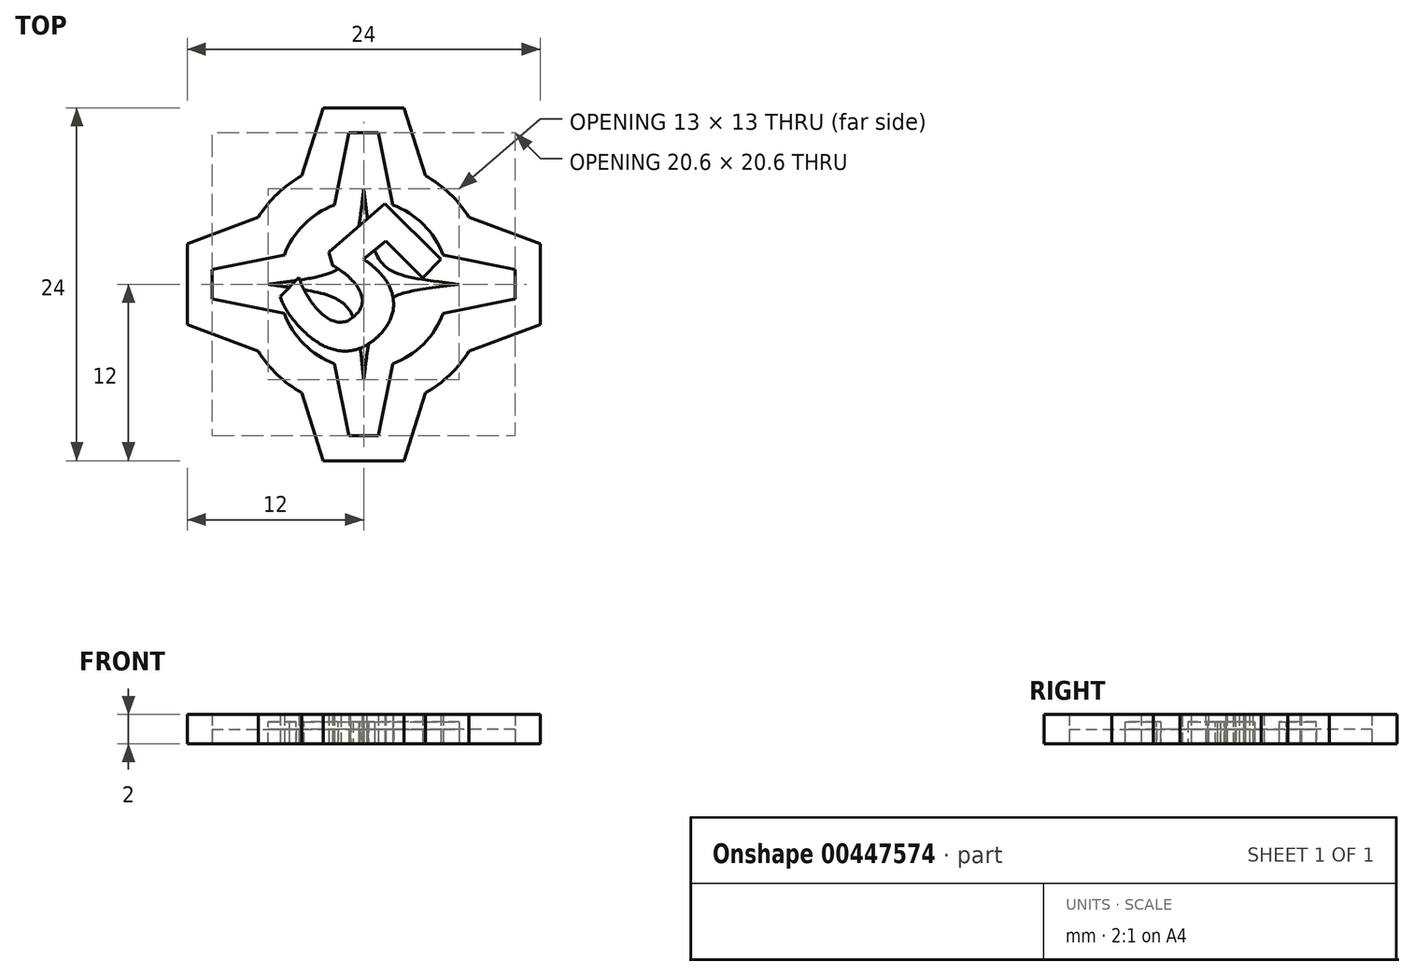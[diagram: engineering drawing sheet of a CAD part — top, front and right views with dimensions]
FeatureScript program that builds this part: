
annotation { "Feature Type Name" : "Feature", "Feature Type Description" : "" }
export const myFeature = defineFeature(function(context is Context, id is Id, definition is map)
    precondition{}
    {
        {
            var Q0;
            Q0=qCreatedBy(makeId("Top.planeOp"),FACE);
            var sketch = newSketch(context, id + "F0", { "sketchPlane" : qUnion([Q0])});
            skArc(sketch, "E0", {"start": v(-4.2, 7.39) * mm, "mid": v(-5.86, 6.16) * mm, "end": v(-7.17, 4.56) * mm});
            skLineSegment(sketch, "E1", {"start": v(-2.75, 12) * mm, "end": v(2.75, 12) * mm});
            skLineSegment(sketch, "E2", {"start": v(2.75, 12) * mm, "end": v(4.2, 7.39) * mm});
            skLineSegment(sketch, "E3", {"start": v(-2.75, 12) * mm, "end": v(-4.2, 7.39) * mm});
            skLineSegment(sketch, "E4", {"start": v(12, 2.75) * mm, "end": v(12, -2.75) * mm});
            skLineSegment(sketch, "E5", {"start": v(12, -2.75) * mm, "end": v(7.17, -4.56) * mm});
            skLineSegment(sketch, "E6", {"start": v(12, 2.75) * mm, "end": v(7.17, 4.56) * mm});
            skLineSegment(sketch, "E7.MirrorCS", {"start": v(-12, 2.75) * mm, "end": v(-7.17, 4.56) * mm});
            skLineSegment(sketch, "E8.MirrorCS", {"start": v(-12, 2.75) * mm, "end": v(-12, -2.75) * mm});
            skLineSegment(sketch, "E9.MirrorCS", {"start": v(-12, -2.75) * mm, "end": v(-7.17, -4.56) * mm});
            skLineSegment(sketch, "E10.MirrorCS", {"start": v(-2.75, -12) * mm, "end": v(-4.2, -7.39) * mm});
            skLineSegment(sketch, "E11.MirrorCS", {"start": v(-2.75, -12) * mm, "end": v(2.75, -12) * mm});
            skLineSegment(sketch, "E12.MirrorCS", {"start": v(2.75, -12) * mm, "end": v(4.2, -7.39) * mm});
            skArc(sketch, "E13", {"start": v(-1.98, 5.4) * mm, "mid": v(-4.07, 4.07) * mm, "end": v(-5.4, 1.98) * mm});
            skArc(sketch, "E14.trimOffspring", {"start": v(-7.17, -4.56) * mm, "mid": v(-5.86, -6.16) * mm, "end": v(-4.2, -7.39) * mm});
            skArc(sketch, "E15.trimOffspring", {"start": v(7.17, 4.56) * mm, "mid": v(5.86, 6.16) * mm, "end": v(4.2, 7.39) * mm});
            skArc(sketch, "E16.trimOffspring", {"start": v(4.2, -7.39) * mm, "mid": v(5.86, -6.16) * mm, "end": v(7.17, -4.56) * mm});
            skLineSegment(sketch, "E17", {"start": v(-1, 10.3) * mm, "end": v(1, 10.3) * mm});
            skLineSegment(sketch, "E18", {"start": v(1, 10.3) * mm, "end": v(1.98, 5.4) * mm});
            skLineSegment(sketch, "E19", {"start": v(-1, 10.3) * mm, "end": v(-1.98, 5.4) * mm});
            skLineSegment(sketch, "E20", {"start": v(10.3, 1) * mm, "end": v(10.3, -1) * mm});
            skLineSegment(sketch, "E21", {"start": v(10.3, -1) * mm, "end": v(5.4, -1.98) * mm});
            skLineSegment(sketch, "E22", {"start": v(10.3, 1) * mm, "end": v(5.4, 1.98) * mm});
            skLineSegment(sketch, "E23.MirrorCS", {"start": v(-1, -10.3) * mm, "end": v(-1.98, -5.4) * mm});
            skLineSegment(sketch, "E24.MirrorCS", {"start": v(-1, -10.3) * mm, "end": v(1, -10.3) * mm});
            skLineSegment(sketch, "E25.MirrorCS", {"start": v(1, -10.3) * mm, "end": v(1.98, -5.4) * mm});
            skLineSegment(sketch, "E26.MirrorCS", {"start": v(-10.3, 1) * mm, "end": v(-5.4, 1.98) * mm});
            skLineSegment(sketch, "E27.MirrorCS", {"start": v(-10.3, 1) * mm, "end": v(-10.3, -1) * mm});
            skLineSegment(sketch, "E28.MirrorCS", {"start": v(-10.3, -1) * mm, "end": v(-5.4, -1.98) * mm});
            skArc(sketch, "E29.trimOffspring", {"start": v(-5.4, -1.98) * mm, "mid": v(-4.07, -4.07) * mm, "end": v(-1.98, -5.4) * mm});
            skArc(sketch, "E30.trimOffspring", {"start": v(1.98, -5.4) * mm, "mid": v(4.07, -4.07) * mm, "end": v(5.4, -1.98) * mm});
            skArc(sketch, "E31.trimOffspring", {"start": v(5.4, 1.98) * mm, "mid": v(4.07, 4.07) * mm, "end": v(1.98, 5.4) * mm});
            skFitSpline(sketch, "E32", {"points": [v(-6.5, 0) * mm, v(0, -6.5) * mm], "startDerivative": vector(17.8, -2.47) * mm, "endDerivative": vector(1.7, -17.03) * mm});
            skFitSpline(sketch, "E33", {"points": [v(0, -6.5) * mm, v(6.5, 0) * mm], "startDerivative": vector(2.16, 17.42) * mm, "endDerivative": vector(17.34, 2.08) * mm});
            skFitSpline(sketch, "E34", {"points": [v(6.5, 0) * mm, v(0, 6.5) * mm], "startDerivative": vector(-17.34, 2.09) * mm, "endDerivative": vector(-2.16, 17.41) * mm});
            skFitSpline(sketch, "E35", {"points": [v(0, 6.5) * mm, v(-6.5, 0) * mm], "startDerivative": vector(-2, -17.27) * mm, "endDerivative": vector(-17.5, -2.23) * mm});
            skText(sketch, "E36", { "text": "5", "fontName": "OpenSans-Bold.ttf"});
            const initialGuessF0  = {"E36": [-0.00644, -0.00063, 0.707, -0.70722, 0.01]};
            skSetInitialGuess(sketch, initialGuessF0);
            skSolve(sketch);
        }
        {
            var Q0;
            Q0=makeQuery(id+"F0.imprint","IMPRINT",FACE,{"disambiguationData":[TD([[makeQuery(id+"F0.imprint","IMPRINT",EDGE,{"derivedFrom":sQuery(id+"F0.wireOp",EDGE,"E0")}),1.0]])]});
            var Q1;
            {var subQ5=sQuery(id+"F0.wireOp",EDGE,"E36.sketch_text.stroke-14");Q1=makeQuery(id+"F0.imprint","IMPRINT",FACE,{"disambiguationData":[TD([[makeQuery(id+"F0.imprint","IMPRINT",EDGE,{"derivedFrom":subQ5}),-1.0]])]});}
            var Q2;
            {var subQ6=sQuery(id+"F0.wireOp",EDGE,"E36.sketch_text.stroke-9");Q2=makeQuery(id+"F0.imprint","IMPRINT",FACE,{"disambiguationData":[TD([[makeQuery(id+"F0.imprint","IMPRINT",EDGE,{"derivedFrom":subQ6}),-1.0]])]});}
            var Q3;
            {var subQ5=sQuery(id+"F0.wireOp",EDGE,"E36.sketch_text.stroke-12");Q3=makeQuery(id+"F0.imprint","IMPRINT",FACE,{"disambiguationData":[TD([[makeQuery(id+"F0.imprint","IMPRINT",EDGE,{"derivedFrom":subQ5}),-1.0]])]});}
            var Q4;
            {var subQ5=sQuery(id+"F0.wireOp",EDGE,"E36.sketch_text.stroke-1");Q4=makeQuery(id+"F0.imprint","IMPRINT",FACE,{"disambiguationData":[TD([[makeQuery(id+"F0.imprint","IMPRINT",EDGE,{"derivedFrom":subQ5}),-1.0]])]});}
            var Q5;
            {var subQ0=sQuery(id+"F0.wireOp",EDGE,"E36.sketch_text.stroke-3");Q5=makeQuery(id+"F0.imprint","IMPRINT",FACE,{"disambiguationData":[TD([[makeQuery(id+"F0.imprint","IMPRINT",EDGE,{"derivedFrom":subQ0}),-1.0]])]});}
            var Q6;
            {var subQ0=sQuery(id+"F0.wireOp",EDGE,"E36.sketch_text.stroke-5");var subQ1=sQuery(id+"F0.wireOp",EDGE,"E32");var subQ2=makeQuery(id+"F0.imprint","INTERSECT",VERTEX,{"derivedFrom":[subQ1,subQ0]});Q6=makeQuery(id+"F0.imprint","IMPRINT",FACE,{"disambiguationData":[TD([[makeQuery(id+"F0.imprint","IMPRINT",EDGE,{"disambiguationData":[TD([[subQ2,-1.0]])],"derivedFrom":subQ1}),1.0]])]});}
            var Q7;
            {var subQ0=sQuery(id+"F0.wireOp",EDGE,"E36.sketch_text.stroke-6");var subQ1=sQuery(id+"F0.wireOp",EDGE,"E35");var subQ2=makeQuery(id+"F0.imprint","INTERSECT",VERTEX,{"derivedFrom":[subQ1,subQ0]});Q7=makeQuery(id+"F0.imprint","IMPRINT",FACE,{"disambiguationData":[TD([[makeQuery(id+"F0.imprint","IMPRINT",EDGE,{"disambiguationData":[TD([[subQ2,-1.0]])],"derivedFrom":subQ1}),-1.0]])]});}
            extrude(context, id + "F1", {"entities" : qUnion([Q0, Q1, Q2, Q3, Q4, Q5, Q6, Q7]), "depth" : 2 * mm});
        }
        {
            var Q0;
            Q0=makeQuery(id+"F0.imprint","IMPRINT",FACE,{"disambiguationData":[TD([[makeQuery(id+"F0.imprint","IMPRINT",EDGE,{"derivedFrom":sQuery(id+"F0.wireOp",EDGE,"E13")}),1.0]])]});
            var Q1;
            {var subQ10=sQuery(id+"F0.wireOp",EDGE,"E20");Q1=makeQuery(id+"F0.imprint","IMPRINT",FACE,{"disambiguationData":[TD([[makeQuery(id+"F0.imprint","IMPRINT",EDGE,{"derivedFrom":subQ10}),-1.0]])]});}
            var Q2;
            {var subQ0=sQuery(id+"F0.wireOp",EDGE,"E36.sketch_text.stroke-14");var subQ1=sQuery(id+"F0.wireOp",EDGE,"E31.trimOffspring");var subQ2=makeQuery(id+"F0.imprint","INTERSECT",VERTEX,{"disambiguationData":[OD(0.0)],"derivedFrom":[subQ1,subQ0]});Q2=makeQuery(id+"F0.imprint","IMPRINT",FACE,{"disambiguationData":[TD([[makeQuery(id+"F0.imprint","IMPRINT",EDGE,{"disambiguationData":[TD([[subQ2,-1.0]])],"derivedFrom":subQ1}),1.0]])]});}
            extrude(context, id + "F2", {"entities" : qUnion([Q0, Q1, Q2]), "depth" : 1 * mm});
        }
        {
            var Q0;
            {var subQ0=sQuery(id+"F0.wireOp",EDGE,"E35");var subQ1=sQuery(id+"F0.wireOp",EDGE,"E34");var subQ2=makeQuery(id+"F0.imprint","INTERSECT",VERTEX,{"derivedFrom":[subQ1,subQ0]});Q0=makeQuery(id+"F0.imprint","IMPRINT",FACE,{"disambiguationData":[TD([[makeQuery(id+"F0.imprint","IMPRINT",EDGE,{"disambiguationData":[TD([[subQ2,1.0]])],"derivedFrom":subQ1}),1.0]])]});}
            var Q1;
            {var subQ0=sQuery(id+"F0.wireOp",EDGE,"E36.sketch_text.stroke-18");Q1=makeQuery(id+"F0.imprint","IMPRINT",FACE,{"disambiguationData":[TD([[makeQuery(id+"F0.imprint","IMPRINT",EDGE,{"derivedFrom":subQ0}),1.0]])]});}
            var Q2;
            {var subQ10=sQuery(id+"F0.wireOp",EDGE,"E36.sketch_text.stroke-9");Q2=makeQuery(id+"F0.imprint","IMPRINT",FACE,{"disambiguationData":[TD([[makeQuery(id+"F0.imprint","IMPRINT",EDGE,{"derivedFrom":subQ10}),1.0]])]});}
            var Q3;
            {var subQ0=sQuery(id+"F0.wireOp",EDGE,"E33");var subQ1=sQuery(id+"F0.wireOp",EDGE,"E32");var subQ2=makeQuery(id+"F0.imprint","INTERSECT",VERTEX,{"derivedFrom":[subQ1,subQ0]});Q3=makeQuery(id+"F0.imprint","IMPRINT",FACE,{"disambiguationData":[TD([[makeQuery(id+"F0.imprint","IMPRINT",EDGE,{"disambiguationData":[TD([[subQ2,1.0]])],"derivedFrom":subQ1}),1.0]])]});}
            var Q4;
            {var subQ0=sQuery(id+"F0.wireOp",EDGE,"E35");var subQ1=sQuery(id+"F0.wireOp",EDGE,"E32");var subQ2=makeQuery(id+"F0.imprint","INTERSECT",VERTEX,{"derivedFrom":[subQ1,subQ0]});Q4=makeQuery(id+"F0.imprint","IMPRINT",FACE,{"disambiguationData":[TD([[makeQuery(id+"F0.imprint","IMPRINT",EDGE,{"disambiguationData":[TD([[subQ2,-1.0]])],"derivedFrom":subQ1}),1.0]])]});}
            extrude(context, id + "F3", {"entities" : qUnion([Q0, Q1, Q2, Q3, Q4]), "depth" : 1.5 * mm});
        }
    });
